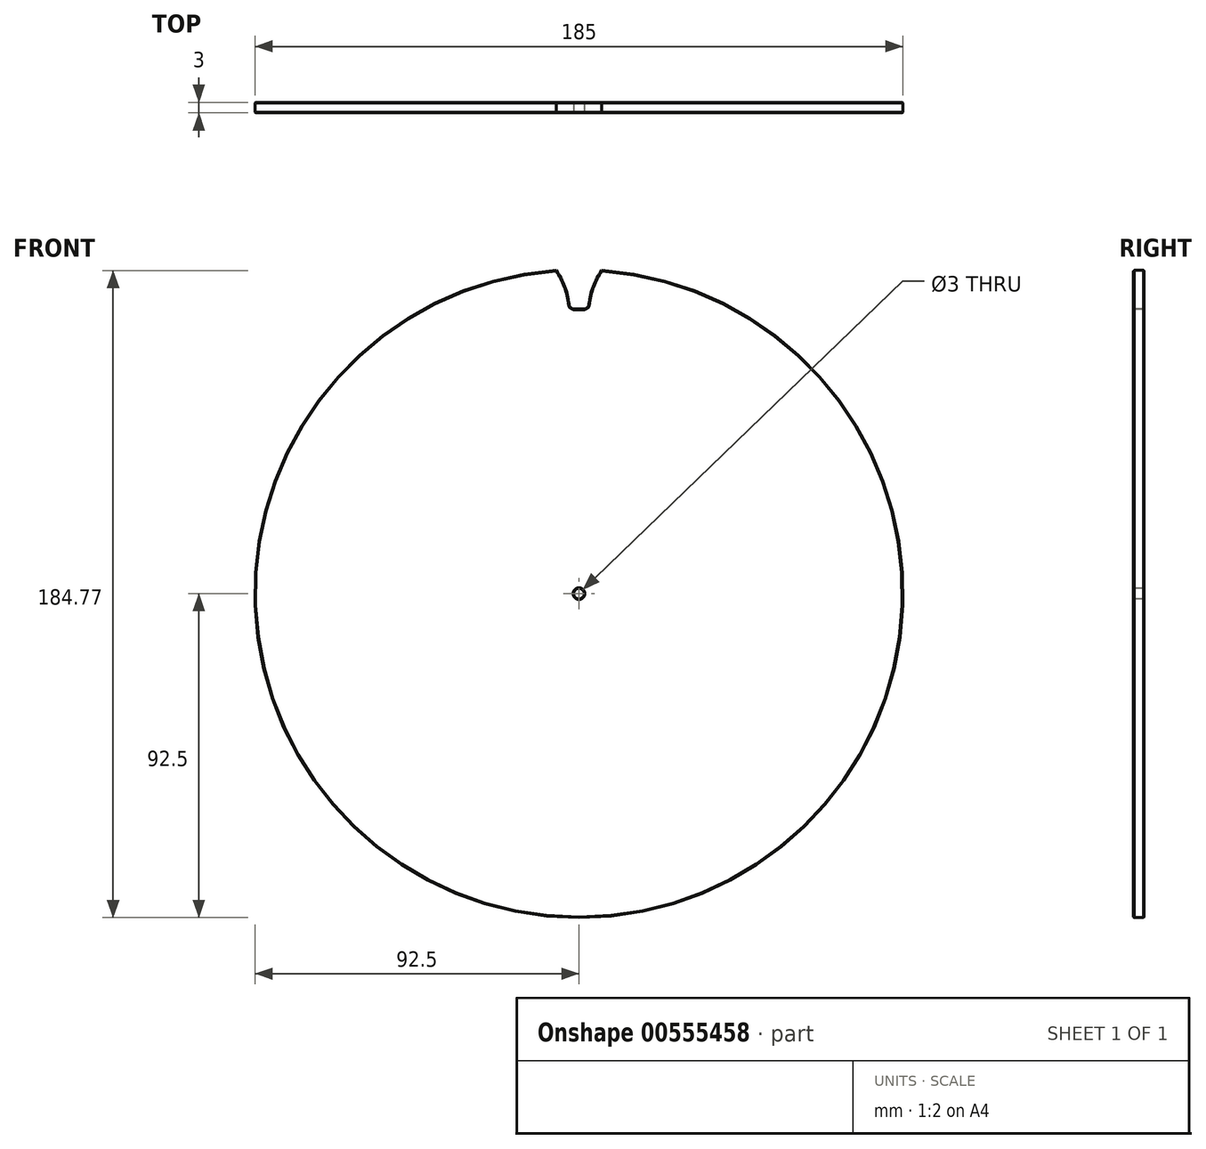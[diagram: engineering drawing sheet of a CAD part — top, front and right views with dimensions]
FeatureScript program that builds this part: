
annotation { "Feature Type Name" : "Feature", "Feature Type Description" : "" }
export const myFeature = defineFeature(function(context is Context, id is Id, definition is map)
    precondition{}
    {
        {
            assignVariable(context, id + "F0", {"name" : "Module", "anyValue" : 5 * mm});
        }
        {
            assignVariable(context, id + "F1", {"name" : "Thickness", "anyValue" : 3 * mm});
        }
        {
            var Q0;
            Q0=qCreatedBy(makeId("Front.planeOp"),FACE);
            var sketch = newSketch(context, id + "F2", { "sketchPlane" : qUnion([Q0])});
            skCircle(sketch, "E0", {"center": v(0, 0) * mm, "radius": 87.5 * mm});
            skCircle(sketch, "E1", {"center": v(0, 0) * mm, "radius": 92.5 * mm});
            skCircle(sketch, "E2", {"center": v(0, 0) * mm, "radius": 81.25 * mm});
            skSolve(sketch);
        }
        {
            var Q0;
            Q0=makeQuery(id+"F2.imprint","IMPRINT",FACE,{"disambiguationData":[TD([[makeQuery(id+"F2.imprint","IMPRINT",EDGE,{"derivedFrom":sQuery(id+"F2.wireOp",EDGE,"E2")}),1.0]])]});
            var Q1;
            Q1=makeQuery(id+"F2.imprint","IMPRINT",FACE,{"disambiguationData":[TD([[makeQuery(id+"F2.imprint","IMPRINT",EDGE,{"derivedFrom":sQuery(id+"F2.wireOp",EDGE,"E0")}),1.0]])]});
            var Q2;
            Q2=makeQuery(id+"F2.imprint","IMPRINT",FACE,{"disambiguationData":[TD([[makeQuery(id+"F2.imprint","IMPRINT",EDGE,{"derivedFrom":sQuery(id+"F2.wireOp",EDGE,"E0")}),-1.0]])]});
            extrude(context, id + "F3", {"entities" : qUnion([Q0, Q1, Q2]), "depth" : getVariable(context, 'Thickness'), "offsetDistance" : 25 * mm, "symmetric" : true});
        }
        {
            var Q0;
            Q0=qCreatedBy(makeId("Front.planeOp"),FACE);
            var sketch = newSketch(context, id + "F4", { "sketchPlane" : qUnion([Q0])});
            skCircle(sketch, "E3", {"center": v(0, 0) * mm, "radius": 1.5 * mm});
            skSolve(sketch);
        }
        {
            var Q0;
            Q0 = qSketchRegion(id + "F4", true);
            extrude(context, id + "F5", {"entities" : qUnion([Q0]), "operationType" : NewBodyOperationType.REMOVE, "endBound" : BoundingType.THROUGH_ALL, "oppositeDirection" : true, "depth" : 25 * mm, "offsetDistance" : 25 * mm, "hasSecondDirection" : true, "secondDirectionBound" : BoundingType.THROUGH_ALL, "secondDirectionOppositeDirection" : false, "secondDirectionDepth" : 25 * mm});
        }
        {
            var Q0;
            Q0=qCreatedBy(makeId("Front.planeOp"),FACE);
            var sketch = newSketch(context, id + "F6", { "sketchPlane" : qUnion([Q0])});
            skLineSegment(sketch, "E4", {"start": v(0, 0) * mm, "end": v(0, 92.5) * mm, "construction": true});
            skArc(sketch, "E5", {"start": v(-2.72, 81.2) * mm, "mid": v(-3.99, 87.58) * mm, "end": v(-7.22, 93.22) * mm});
            skArc(sketch, "E6.MirrorCS", {"start": v(2.72, 81.2) * mm, "mid": v(3.99, 87.58) * mm, "end": v(7.22, 93.22) * mm});
            skArc(sketch, "E7.0", {"start": v(2.72, 81.2) * mm, "mid": v(0, 81.25) * mm, "end": v(-2.72, 81.2) * mm});
            skArc(sketch, "E8.0", {"start": v(7.22, 93.22) * mm, "mid": v(0, 93.5) * mm, "end": v(-7.22, 93.22) * mm});
            skLineSegment(sketch, "E9", {"start": v(-3.93, 87.41) * mm, "end": v(3.93, 87.41) * mm, "construction": true});
            skLineSegment(sketch, "E10", {"start": v(0, 0) * mm, "end": v(-2.72, 81.2) * mm, "construction": true});
            skLineSegment(sketch, "E11", {"start": v(0, 76.63) * mm, "end": v(-6.07, 93.3) * mm, "construction": true});
            skLineSegment(sketch, "E12", {"start": v(0, 0) * mm, "end": v(8.3, 92.13) * mm, "construction": true});
            skLineSegment(sketch, "E13", {"start": v(3.93, 87.41) * mm, "end": v(11.75, 86.7) * mm, "construction": true});
            skSolve(sketch);
        }
        {
            var Q0;
            Q0 = qSketchRegion(id + "F6", true);
            extrude(context, id + "F7", {"entities" : qUnion([Q0]), "operationType" : NewBodyOperationType.REMOVE, "endBound" : BoundingType.THROUGH_ALL, "oppositeDirection" : true, "depth" : 25 * mm, "offsetDistance" : 25 * mm, "hasSecondDirection" : true, "secondDirectionBound" : BoundingType.THROUGH_ALL, "secondDirectionOppositeDirection" : false, "secondDirectionDepth" : 25 * mm});
        }
        {
            var Q0;
            Q0=makeQuery(id+"F7.boolean.opBoolean","COPY",EDGE,{"derivedFrom":makeQuery(id+"F7.opExtrude","SWEPT_EDGE",EDGE,{"disambiguationData":[OSD([sQuery(id+"F6.wireOp",EDGE,"E5"),sQuery(id+"F6.wireOp",EDGE,"E7.0")])]})});
            var Q1;
            Q1=makeQuery(id+"F7.boolean.opBoolean","COPY",EDGE,{"derivedFrom":makeQuery(id+"F7.opExtrude","SWEPT_EDGE",EDGE,{"disambiguationData":[OSD([sQuery(id+"F6.wireOp",EDGE,"E6.MirrorCS"),sQuery(id+"F6.wireOp",EDGE,"E7.0")])]})});
            fillet(context, id + "F8", {"entities" : qUnion([Q0, Q1]), "radius" : .3 * getVariable(context, 'Module'), "tangentPropagation" : true, "allowEdgeOverflow" : false});
        }
        {
            var Q0;
            Q0=makeQuery(id+"F3.opExtrude","CAP_FACE",FACE,{"disambiguationData":[OSD([sQuery(id+"F2.wireOp",EDGE,"E1")])],"isStart":false});
            var Q1;
            Q1=makeQuery(id+"F3.opExtrude","CAP_FACE",FACE,{"disambiguationData":[OSD([sQuery(id+"F2.wireOp",EDGE,"E1")])],"isStart":true});
            chamfer(context, id + "F9", {"entities" : qUnion([Q0, Q1]), "width" : 0.18 * mm, "tangentPropagation" : true});
        }
    });
